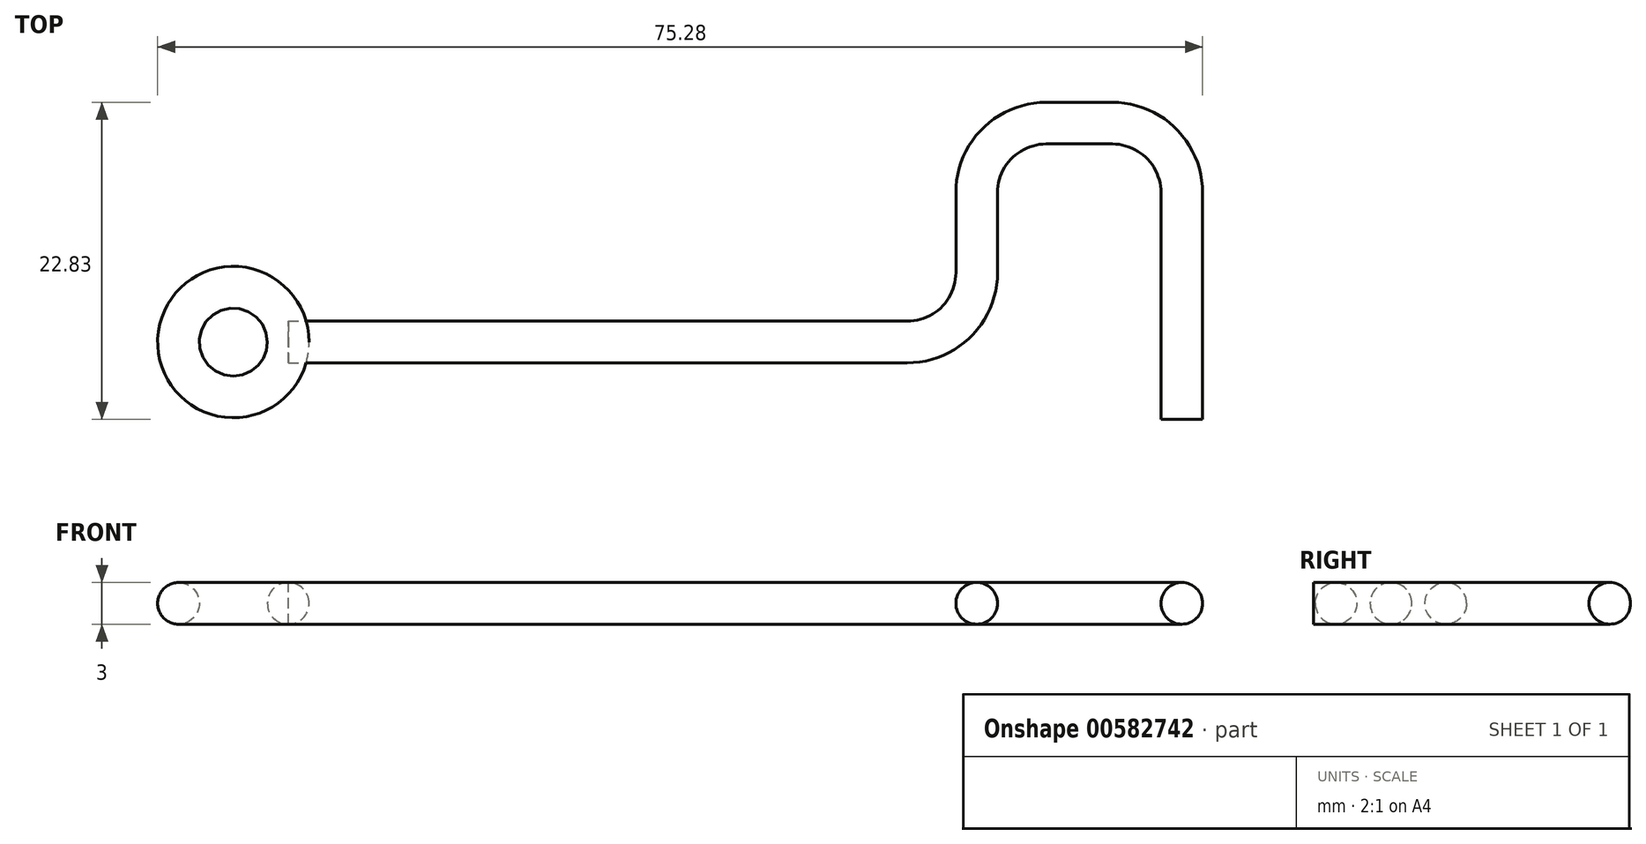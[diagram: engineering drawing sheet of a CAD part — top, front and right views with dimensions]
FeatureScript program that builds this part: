
annotation { "Feature Type Name" : "Feature", "Feature Type Description" : "" }
export const myFeature = defineFeature(function(context is Context, id is Id, definition is map)
    precondition{}
    {
        {
            var Q0;
            Q0=qCreatedBy(makeId("Top.planeOp"),FACE);
            var sketch = newSketch(context, id + "F0", { "sketchPlane" : qUnion([Q0])});
            skLineSegment(sketch, "E0", {"start": v(0, 0) * mm, "end": v(44.6, 0) * mm});
            skLineSegment(sketch, "E1", {"start": v(49.6, 5) * mm, "end": v(49.6, 10.76) * mm});
            skLineSegment(sketch, "E2", {"start": v(54.6, 15.76) * mm, "end": v(59.37, 15.76) * mm});
            skLineSegment(sketch, "E3", {"start": v(64.37, 10.76) * mm, "end": v(64.37, -5.57) * mm});
            skArc(sketch, "E4.filletArc", {"start": v(44.6, 0) * mm, "mid": v(48.13, 1.46) * mm, "end": v(49.6, 5) * mm});
            skPoint(sketch, "E5.visualSharp", {"position": v(49.6, 15.76) * mm});
            skArc(sketch, "E5.filletArc", {"start": v(54.6, 15.76) * mm, "mid": v(51.06, 14.3) * mm, "end": v(49.6, 10.76) * mm});
            skPoint(sketch, "E6.visualSharp", {"position": v(64.37, 15.76) * mm});
            skArc(sketch, "E6.filletArc", {"start": v(64.37, 10.76) * mm, "mid": v(62.9, 14.3) * mm, "end": v(59.37, 15.76) * mm});
            skCircle(sketch, "E7", {"center": v(-3.95, 0) * mm, "radius": 3.95 * mm});
            skSolve(sketch);
        }
        {
            var Q0;
            Q0=qCreatedBy(makeId("Right.planeOp"),FACE);
            var sketch = newSketch(context, id + "F1", { "sketchPlane" : qUnion([Q0])});
            skCircle(sketch, "E8", {"center": v(0, 0) * mm, "radius": 1.5 * mm});
            skSolve(sketch);
        }
        {
            var Q0;
            Q0=makeQuery(id+"F1.imprint","IMPRINT",FACE,{"disambiguationData":[TD([[makeQuery(id+"F1.imprint","IMPRINT",EDGE,{"derivedFrom":sQuery(id+"F1.wireOp",EDGE,"E8")}),1.0]])]});
            var Q1;
            Q1=sQuery(id+"F0.wireOp",EDGE,"E0");
            var Q2;
            Q2=sQuery(id+"F0.wireOp",EDGE,"E4.filletArc");
            var Q3;
            Q3=sQuery(id+"F0.wireOp",EDGE,"E1");
            var Q4;
            Q4=sQuery(id+"F0.wireOp",EDGE,"E5.filletArc");
            var Q5;
            Q5=sQuery(id+"F0.wireOp",EDGE,"E2");
            var Q6;
            Q6=sQuery(id+"F0.wireOp",EDGE,"E6.filletArc");
            var Q7;
            Q7=sQuery(id+"F0.wireOp",EDGE,"E3");
            sweep(context, id + "F2", {"profiles" : qUnion([Q0]), "path" : qUnion([Q1, Q2, Q3, Q4, Q5, Q6, Q7])});
        }
        {
            var Q0;
            Q0=qCreatedBy(makeId("Front.planeOp"),FACE);
            var sketch = newSketch(context, id + "F3", { "sketchPlane" : qUnion([Q0])});
            skCircle(sketch, "E9", {"center": v(0, 0) * mm, "radius": 1.5 * mm});
            skSolve(sketch);
        }
        {
            var Q0;
            Q0=makeQuery(id+"F3.imprint","IMPRINT",FACE,{"disambiguationData":[TD([[makeQuery(id+"F3.imprint","IMPRINT",EDGE,{"derivedFrom":sQuery(id+"F3.wireOp",EDGE,"E9")}),1.0]])]});
            var Q1;
            Q1=sQuery(id+"F0.wireOp",EDGE,"E7");
            sweep(context, id + "F4", {"profiles" : qUnion([Q0]), "path" : qUnion([Q1])});
        }
    });
